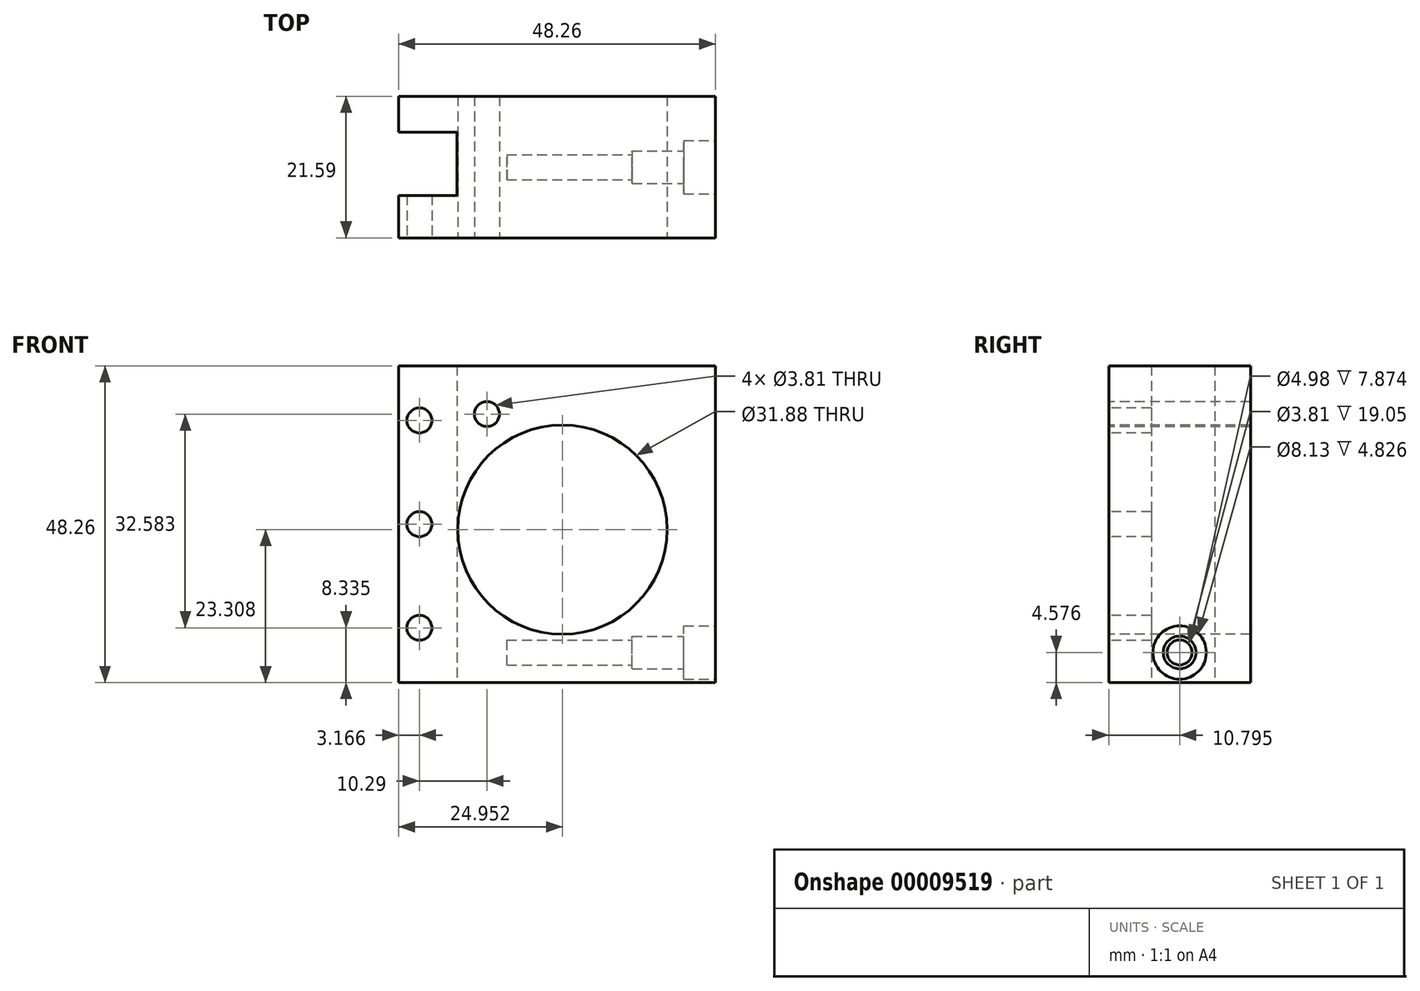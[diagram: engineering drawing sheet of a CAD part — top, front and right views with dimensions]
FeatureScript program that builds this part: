
annotation { "Feature Type Name" : "Feature", "Feature Type Description" : "" }
export const myFeature = defineFeature(function(context is Context, id is Id, definition is map)
    precondition{}
    {
        {
            var Q0;
            Q0=qCreatedBy(makeId("Front.planeOp"),FACE);
            var sketch = newSketch(context, id + "F0", { "sketchPlane" : qUnion([Q0])});
            skLineSegment(sketch, "E0.bottom", {"start": v(-180.25, 28.04) * mm, "end": v(-132, 28.04) * mm});
            skLineSegment(sketch, "E0.top", {"start": v(-180.25, -20.22) * mm, "end": v(-149.6, -20.22) * mm});
            skLineSegment(sketch, "E0.left", {"start": v(-180.25, 28.04) * mm, "end": v(-180.25, -20.22) * mm});
            skLineSegment(sketch, "E0.right", {"start": v(-132, 28.04) * mm, "end": v(-132, -20.22) * mm});
            skCircle(sketch, "E1", {"center": v(-155.3, 3.09) * mm, "radius": 15.94 * mm});
            skLineSegment(sketch, "E2", {"start": v(-155.3, 3.09) * mm, "end": v(-130.34, 3.09) * mm, "construction": true});
            skLineSegment(sketch, "E3", {"start": v(-155.3, 3.09) * mm, "end": v(-155.3, -21.87) * mm, "construction": true});
            skLineSegment(sketch, "E4", {"start": v(-173.65, -20.22) * mm, "end": v(-173.65, 28.04) * mm, "construction": true});
            skLineSegment(sketch, "E5", {"start": v(-177.08, 28.04) * mm, "end": v(-177.08, -20.22) * mm, "construction": true});
            skCircle(sketch, "E6", {"center": v(-177.08, 19.73) * mm, "radius": 1.9 * mm});
            skCircle(sketch, "E7", {"center": v(-177.08, 3.91) * mm, "radius": 1.9 * mm});
            skCircle(sketch, "E8", {"center": v(-177.08, -11.89) * mm, "radius": 1.9 * mm});
            skCircle(sketch, "E9", {"center": v(-166.8, 20.7) * mm, "radius": 1.9 * mm});
            skCircle(sketch, "E10", {"center": v(-155.3, 3.09) * mm, "radius": 4.97 * mm});
            skCircle(sketch, "E11", {"center": v(-155.3, 3.09) * mm, "radius": 7.14 * mm});
            skLineSegment(sketch, "E12.trimOffspring", {"start": v(-146.3, -20.22) * mm, "end": v(-132, -20.22) * mm});
            skCircle(sketch, "E13", {"center": v(-166.8, 20.7) * mm, "radius": 2.45 * mm});
            skLineSegment(sketch, "E14", {"start": v(-149.6, -20.22) * mm, "end": v(-146.3, -20.22) * mm});
            skSolve(sketch);
        }
        {
            var Q0;
            Q0=makeQuery(id+"F0.imprint","IMPRINT",FACE,{"disambiguationData":[TD([[makeQuery(id+"F0.imprint","IMPRINT",EDGE,{"derivedFrom":sQuery(id+"F0.wireOp",EDGE,"E0.bottom")}),-1.0]])]});
            var Q1;
            Q1=makeQuery(id+"F0.imprint","IMPRINT",FACE,{"disambiguationData":[TD([[makeQuery(id+"F0.imprint","IMPRINT",EDGE,{"derivedFrom":sQuery(id+"F0.wireOp",EDGE,"E9")}),1.0]])]});
            var Q2;
            Q2=makeQuery(id+"F0.imprint","IMPRINT",FACE,{"disambiguationData":[TD([[makeQuery(id+"F0.imprint","IMPRINT",EDGE,{"derivedFrom":sQuery(id+"F0.wireOp",EDGE,"E6")}),1.0]])]});
            var Q3;
            Q3=makeQuery(id+"F0.imprint","IMPRINT",FACE,{"disambiguationData":[TD([[makeQuery(id+"F0.imprint","IMPRINT",EDGE,{"derivedFrom":sQuery(id+"F0.wireOp",EDGE,"E7")}),1.0]])]});
            var Q4;
            Q4=makeQuery(id+"F0.imprint","IMPRINT",FACE,{"disambiguationData":[TD([[makeQuery(id+"F0.imprint","IMPRINT",EDGE,{"derivedFrom":sQuery(id+"F0.wireOp",EDGE,"E8")}),1.0]])]});
            var Q5;
            Q5=makeQuery(id+"F0.imprint","IMPRINT",FACE,{"disambiguationData":[TD([[makeQuery(id+"F0.imprint","IMPRINT",EDGE,{"derivedFrom":sQuery(id+"F0.wireOp",EDGE,"E9")}),-1.0]])]});
            var Q6;
            {var subQ1=sQuery(id+"F0.wireOp",EDGE,"2551a94f-3a1d-4b0e-8204-0523b05fb9c7");Q6=makeQuery(id+"F0.imprint","IMPRINT",FACE,{"disambiguationData":[TD([[makeQuery(id+"F0.imprint","IMPRINT",EDGE,{"derivedFrom":subQ1}),1.0]])]});}
            extrude(context, id + "F1", {"entities" : qUnion([Q0, Q1, Q2, Q3, Q4, Q5, Q6]), "oppositeDirection" : true, "depth" : 21.59 * mm});
        }
        {
            var Q0;
            Q0=makeQuery(id+"F0.imprint","IMPRINT",FACE,{"disambiguationData":[TD([[makeQuery(id+"F0.imprint","IMPRINT",EDGE,{"derivedFrom":sQuery(id+"F0.wireOp",EDGE,"E11")}),-1.0]])]});
            var Q1;
            Q1=makeQuery(id+"F0.imprint","IMPRINT",FACE,{"disambiguationData":[TD([[makeQuery(id+"F0.imprint","IMPRINT",EDGE,{"derivedFrom":sQuery(id+"F0.wireOp",EDGE,"E10")}),-1.0]])]});
            var Q2;
            Q2=makeQuery(id+"F0.imprint","IMPRINT",FACE,{"disambiguationData":[TD([[makeQuery(id+"F0.imprint","IMPRINT",EDGE,{"derivedFrom":sQuery(id+"F0.wireOp",EDGE,"E10")}),1.0]])]});
            extrude(context, id + "F2", {"entities" : qUnion([Q0, Q1, Q2]), "oppositeDirection" : true, "depth" : 41.4 * mm});
        }
        {
            var Q0;
            Q0=makeQuery(id+"F0.imprint","IMPRINT",FACE,{"disambiguationData":[TD([[makeQuery(id+"F0.imprint","IMPRINT",EDGE,{"derivedFrom":sQuery(id+"F0.wireOp",EDGE,"E10")}),1.0]])]});
            extrude(context, id + "F3", {"entities" : qUnion([Q0]), "operationType" : NewBodyOperationType.REMOVE, "endBound" : BoundingType.UP_TO_NEXT, "oppositeDirection" : true, "depth" : 25.4 * mm});
        }
        {
            var Q0;
            Q0=makeQuery(id+"F0.imprint","IMPRINT",FACE,{"disambiguationData":[TD([[makeQuery(id+"F0.imprint","IMPRINT",EDGE,{"derivedFrom":sQuery(id+"F0.wireOp",EDGE,"E10")}),-1.0]])]});
            extrude(context, id + "F4", {"entities" : qUnion([Q0]), "operationType" : NewBodyOperationType.REMOVE, "oppositeDirection" : true, "depth" : 3 / 203.2 * mm});
        }
        {
            var Q0;
            Q0=makeQuery(id+"F1.opExtrude","SWEPT_FACE",FACE,{"disambiguationData":[OSD([sQuery(id+"F0.wireOp",EDGE,"E0.top")])]});
            var sketch = newSketch(context, id + "F5", { "sketchPlane" : qUnion([Q0])});
            skLineSegment(sketch, "E15.0", {"start": v(-180.25, -21.59) * mm, "end": v(-180.25, -16.13) * mm, "construction": true});
            skLineSegment(sketch, "E16.0", {"start": v(-180.25, 0) * mm, "end": v(-149.6, 0) * mm, "construction": true});
            skLineSegment(sketch, "E17.0", {"start": v(-180.25, -21.59) * mm, "end": v(-180.25, -21.59) * mm});
            skLineSegment(sketch, "E18.bottom", {"start": v(-180.25, -6.48) * mm, "end": v(-171.36, -6.48) * mm});
            skLineSegment(sketch, "E18.top", {"start": v(-180.25, -16.13) * mm, "end": v(-171.36, -16.13) * mm});
            skLineSegment(sketch, "E18.left", {"start": v(-180.25, -6.48) * mm, "end": v(-180.25, -16.13) * mm});
            skLineSegment(sketch, "E18.right", {"start": v(-171.36, -6.48) * mm, "end": v(-171.36, -16.13) * mm});
            skLineSegment(sketch, "E19", {"start": v(-180.25, -6.48) * mm, "end": v(-180.25, 0) * mm, "construction": true});
            skLineSegment(sketch, "E20", {"start": v(-180.25, -16.13) * mm, "end": v(-180.25, -6.48) * mm, "construction": true});
            skLineSegment(sketch, "E21.0", {"start": v(-132, 0) * mm, "end": v(-132, 0) * mm});
            skLineSegment(sketch, "E22.0", {"start": v(-132, -21.59) * mm, "end": v(-132, -21.59) * mm});
            skLineSegment(sketch, "E23", {"start": v(-136.82, 0) * mm, "end": v(-136.82, -21.59) * mm, "construction": true});
            skLineSegment(sketch, "E24", {"start": v(-163.74, 0) * mm, "end": v(-163.74, -21.59) * mm, "construction": true});
            skLineSegment(sketch, "E25", {"start": v(-162.22, 0) * mm, "end": v(-162.22, -21.59) * mm, "construction": true});
            skSolve(sketch);
        }
        {
            var Q0;
            Q0=makeQuery(id+"F5.imprint","IMPRINT",FACE,{"disambiguationData":[TD([[makeQuery(id+"F5.imprint","IMPRINT",EDGE,{"derivedFrom":sQuery(id+"F5.wireOp",EDGE,"E18.bottom")}),-1.0]])]});
            extrude(context, id + "F6", {"entities" : qUnion([Q0]), "operationType" : NewBodyOperationType.REMOVE, "endBound" : BoundingType.UP_TO_NEXT, "oppositeDirection" : true, "depth" : 25.4 * mm});
        }
        {
            var Q0;
            Q0=makeQuery(id+"F0.imprint","IMPRINT",FACE,{"disambiguationData":[TD([[makeQuery(id+"F0.imprint","IMPRINT",EDGE,{"derivedFrom":sQuery(id+"F0.wireOp",EDGE,"E9")}),1.0]])]});
            extrude(context, id + "F7", {"entities" : qUnion([Q0]), "operationType" : NewBodyOperationType.REMOVE, "endBound" : BoundingType.UP_TO_NEXT, "oppositeDirection" : true, "depth" : 25.4 * mm});
        }
        {
            var Q0;
            Q0=makeQuery(id+"F0.imprint","IMPRINT",FACE,{"disambiguationData":[TD([[makeQuery(id+"F0.imprint","IMPRINT",EDGE,{"derivedFrom":sQuery(id+"F0.wireOp",EDGE,"E6")}),1.0]])]});
            var Q1;
            Q1=makeQuery(id+"F0.imprint","IMPRINT",FACE,{"disambiguationData":[TD([[makeQuery(id+"F0.imprint","IMPRINT",EDGE,{"derivedFrom":sQuery(id+"F0.wireOp",EDGE,"E7")}),1.0]])]});
            var Q2;
            Q2=makeQuery(id+"F0.imprint","IMPRINT",FACE,{"disambiguationData":[TD([[makeQuery(id+"F0.imprint","IMPRINT",EDGE,{"derivedFrom":sQuery(id+"F0.wireOp",EDGE,"E8")}),1.0]])]});
            extrude(context, id + "F8", {"entities" : qUnion([Q0, Q1, Q2]), "operationType" : NewBodyOperationType.REMOVE, "endBound" : BoundingType.UP_TO_NEXT, "oppositeDirection" : true, "depth" : 25.4 * mm});
        }
        {
            var Q0;
            Q0=makeQuery(id+"F1.opExtrude","SWEPT_FACE",FACE,{"disambiguationData":[OSD([sQuery(id+"F0.wireOp",EDGE,"E0.right")])]});
            var sketch = newSketch(context, id + "F9", { "sketchPlane" : qUnion([Q0])});
            skLineSegment(sketch, "E26", {"start": v(12.7, -30.22) * mm, "end": v(12.7, 42.02) * mm, "construction": true});
            skLineSegment(sketch, "E27", {"start": v(0, -15.64) * mm, "end": v(21.59, -15.64) * mm, "construction": true});
            skCircle(sketch, "E28", {"center": v(10.8, -15.64) * mm, "radius": 4.06 * mm});
            skCircle(sketch, "E29", {"center": v(10.8, -15.64) * mm, "radius": 1.9 * mm});
            skCircle(sketch, "E30", {"center": v(10.8, -15.64) * mm, "radius": 2.49 * mm});
            skSolve(sketch);
        }
        {
            var Q0;
            Q0=makeQuery(id+"F9.imprint","IMPRINT",FACE,{"disambiguationData":[TD([[makeQuery(id+"F9.imprint","IMPRINT",EDGE,{"derivedFrom":sQuery(id+"F9.wireOp",EDGE,"E29")}),1.0]])]});
            extrude(context, id + "F10", {"entities" : qUnion([Q0]), "operationType" : NewBodyOperationType.REMOVE, "oppositeDirection" : true, "depth" : 31.75 * mm});
        }
        {
            var Q0;
            Q0=makeQuery(id+"F9.imprint","IMPRINT",FACE,{"disambiguationData":[TD([[makeQuery(id+"F9.imprint","IMPRINT",EDGE,{"derivedFrom":sQuery(id+"F9.wireOp",EDGE,"E29")}),-1.0]])]});
            extrude(context, id + "F11", {"entities" : qUnion([Q0]), "operationType" : NewBodyOperationType.REMOVE, "oppositeDirection" : true, "depth" : 12.7 * mm});
        }
        {
            var Q0;
            Q0=makeQuery(id+"F9.imprint","IMPRINT",FACE,{"disambiguationData":[TD([[makeQuery(id+"F9.imprint","IMPRINT",EDGE,{"derivedFrom":sQuery(id+"F9.wireOp",EDGE,"E28")}),1.0]])]});
            extrude(context, id + "F12", {"entities" : qUnion([Q0]), "operationType" : NewBodyOperationType.REMOVE, "oppositeDirection" : true, "depth" : 4.83 * mm});
        }
        {
            var Q0;
            Q0=makeQuery(id+"F2.opExtrude","SWEPT_BODY",BODY,{"disambiguationData":[OSD([sQuery(id+"F0.wireOp",EDGE,"E1")])]});
            deleteBodies(context, id + "F13", {"entities" : qUnion([Q0])});
        }
    });
